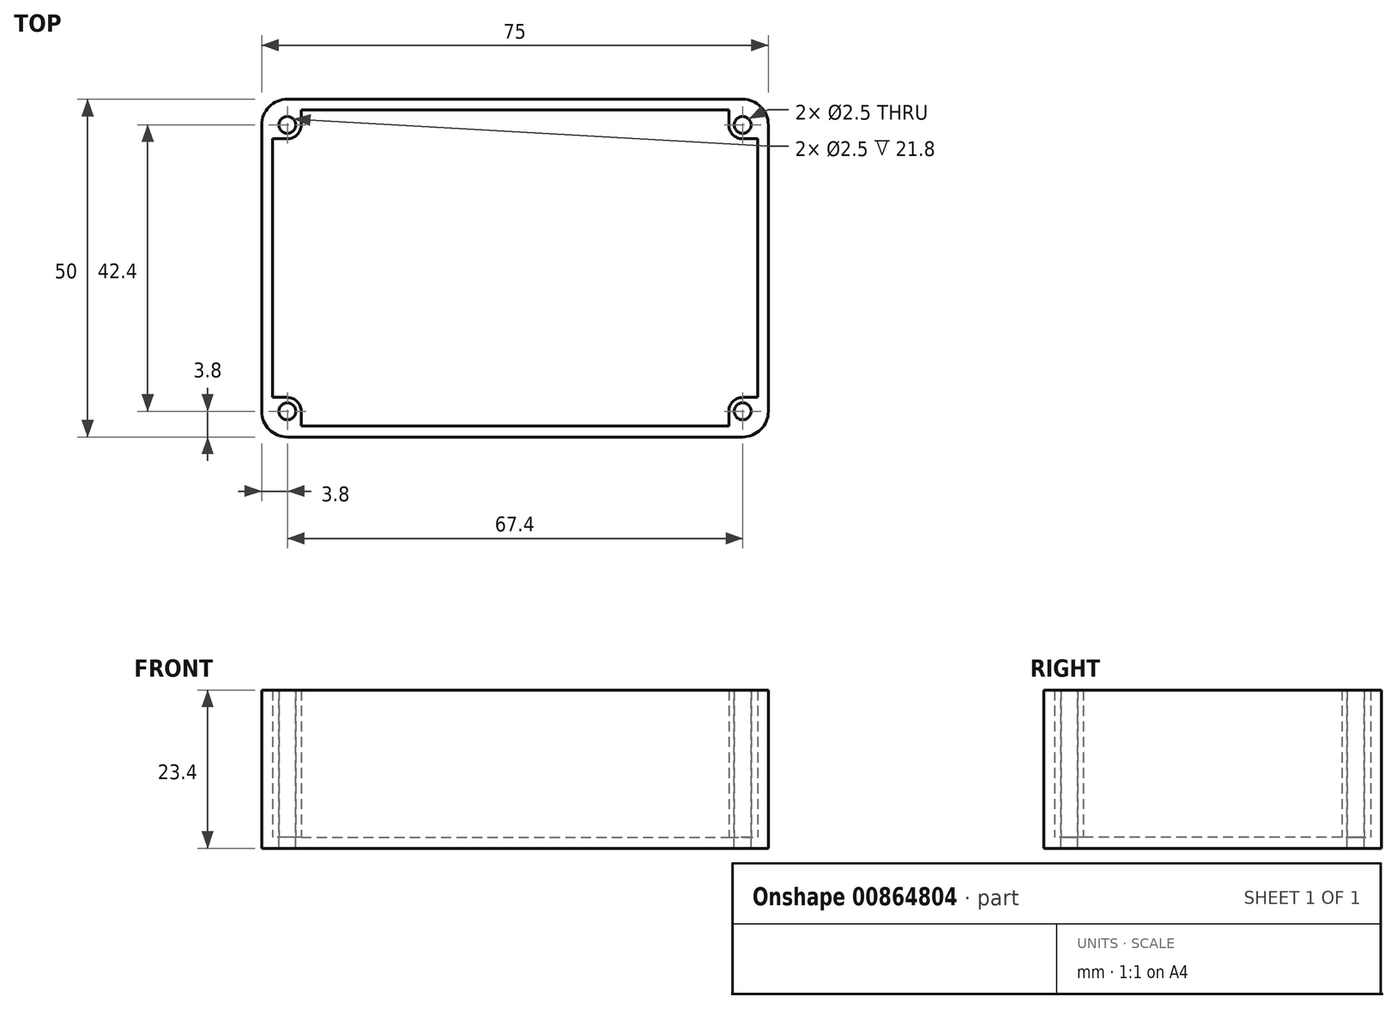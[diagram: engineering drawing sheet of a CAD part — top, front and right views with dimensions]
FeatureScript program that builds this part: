
annotation { "Feature Type Name" : "Feature", "Feature Type Description" : "" }
export const myFeature = defineFeature(function(context is Context, id is Id, definition is map)
    precondition{}
    {
        {
            assignVariable(context, id + "F0", {"name" : "height", "anyValue" : 25});
        }
        {
            assignVariable(context, id + "F1", {"name" : "thickness", "anyValue" : 1.6});
        }
        {
            var Q0;
            Q0=qCreatedBy(makeId("Top.planeOp"),FACE);
            var sketch = newSketch(context, id + "F2", { "sketchPlane" : qUnion([Q0])});
            skLineSegment(sketch, "E0", {"start": v(-37.5, 25) * mm, "end": v(37.5, 25) * mm, "construction": true});
            skLineSegment(sketch, "E1", {"start": v(-37.5, 25) * mm, "end": v(-37.5, -25) * mm, "construction": true});
            skLineSegment(sketch, "E2", {"start": v(-37.5, -25) * mm, "end": v(37.5, -25) * mm, "construction": true});
            skLineSegment(sketch, "E3", {"start": v(37.5, -25) * mm, "end": v(37.5, 25) * mm, "construction": true});
            skLineSegment(sketch, "E4", {"start": v(0, 25) * mm, "end": v(0, 0) * mm, "construction": true});
            skLineSegment(sketch, "E5", {"start": v(0, 0) * mm, "end": v(37.5, 0) * mm, "construction": true});
            skLineSegment(sketch, "E6", {"start": v(0, 0) * mm, "end": v(0, -25) * mm, "construction": true});
            skLineSegment(sketch, "E7", {"start": v(-37.5, 0) * mm, "end": v(0, 0) * mm, "construction": true});
            skLineSegment(sketch, "E8", {"start": v(-33.7, 25) * mm, "end": v(-33.7, -25) * mm, "construction": true});
            skLineSegment(sketch, "E9", {"start": v(-37.5, 21.2) * mm, "end": v(37.5, 21.2) * mm, "construction": true});
            skCircle(sketch, "E10", {"center": v(-33.7, 21.2) * mm, "radius": 1.25 * mm});
            skArc(sketch, "E11", {"start": v(-33.7, 25) * mm, "mid": v(-36.39, 23.89) * mm, "end": v(-37.5, 21.2) * mm});
            skLineSegment(sketch, "E12", {"start": v(-33.7, 25) * mm, "end": v(0, 25) * mm});
            skLineSegment(sketch, "E13", {"start": v(-37.5, 21.2) * mm, "end": v(-37.5, 0) * mm});
            skLineSegment(sketch, "E14", {"start": v(0, 23.4) * mm, "end": v(-31.65, 23.4) * mm});
            skLineSegment(sketch, "E15", {"start": v(-35.9, 19.15) * mm, "end": v(-35.9, 0) * mm});
            skArc(sketch, "E16", {"start": v(-33.7, 19.15) * mm, "mid": v(-32.25, 19.75) * mm, "end": v(-31.65, 21.2) * mm});
            skLineSegment(sketch, "E17", {"start": v(-31.65, 21.2) * mm, "end": v(-31.65, 23.4) * mm});
            skLineSegment(sketch, "E18", {"start": v(-33.7, 19.15) * mm, "end": v(-35.9, 19.15) * mm});
            skCircle(sketch, "E19.MirrorC", {"center": v(33.7, 21.2) * mm, "radius": 1.25 * mm});
            skArc(sketch, "E20.MirrorCS", {"start": v(33.7, 19.15) * mm, "mid": v(32.25, 19.75) * mm, "end": v(31.65, 21.2) * mm});
            skLineSegment(sketch, "E21.MirrorCS", {"start": v(33.7, 19.15) * mm, "end": v(35.9, 19.15) * mm});
            skLineSegment(sketch, "E22.MirrorCS", {"start": v(35.9, 19.15) * mm, "end": v(35.9, 0) * mm});
            skLineSegment(sketch, "E23.MirrorCS", {"start": v(31.65, 21.2) * mm, "end": v(31.65, 23.4) * mm});
            skLineSegment(sketch, "E24.MirrorCS", {"start": v(0, 23.4) * mm, "end": v(31.65, 23.4) * mm});
            skArc(sketch, "E25.MirrorCS", {"start": v(33.7, 25) * mm, "mid": v(36.39, 23.89) * mm, "end": v(37.5, 21.2) * mm});
            skLineSegment(sketch, "E26.MirrorCS", {"start": v(33.7, 25) * mm, "end": v(0, 25) * mm});
            skLineSegment(sketch, "E27.MirrorCS", {"start": v(37.5, 21.2) * mm, "end": v(37.5, 0) * mm});
            skLineSegment(sketch, "E28.MirrorCS", {"start": v(-37.5, -21.2) * mm, "end": v(-37.5, 0) * mm});
            skLineSegment(sketch, "E29.MirrorCS", {"start": v(-33.7, -25) * mm, "end": v(0, -25) * mm});
            skLineSegment(sketch, "E30.MirrorCS", {"start": v(37.5, -21.2) * mm, "end": v(37.5, 0) * mm});
            skLineSegment(sketch, "E31.MirrorCS", {"start": v(33.7, -25) * mm, "end": v(0, -25) * mm});
            skLineSegment(sketch, "E32.MirrorCS", {"start": v(33.7, -19.15) * mm, "end": v(35.9, -19.15) * mm});
            skCircle(sketch, "E33.MirrorC", {"center": v(33.7, -21.2) * mm, "radius": 1.25 * mm});
            skArc(sketch, "E34.MirrorCS", {"start": v(-33.7, -25) * mm, "mid": v(-36.39, -23.89) * mm, "end": v(-37.5, -21.2) * mm});
            skLineSegment(sketch, "E35.MirrorCS", {"start": v(-35.9, -19.15) * mm, "end": v(-35.9, 0) * mm});
            skLineSegment(sketch, "E36.MirrorCS", {"start": v(-31.65, -21.2) * mm, "end": v(-31.65, -23.4) * mm});
            skLineSegment(sketch, "E37.MirrorCS", {"start": v(-33.7, -19.15) * mm, "end": v(-35.9, -19.15) * mm});
            skLineSegment(sketch, "E38.MirrorCS", {"start": v(0, -23.4) * mm, "end": v(31.65, -23.4) * mm});
            skLineSegment(sketch, "E39.MirrorCS", {"start": v(31.65, -21.2) * mm, "end": v(31.65, -23.4) * mm});
            skArc(sketch, "E40.MirrorCS", {"start": v(33.7, -19.15) * mm, "mid": v(32.25, -19.75) * mm, "end": v(31.65, -21.2) * mm});
            skArc(sketch, "E41.MirrorCS", {"start": v(-33.7, -19.15) * mm, "mid": v(-32.25, -19.75) * mm, "end": v(-31.65, -21.2) * mm});
            skLineSegment(sketch, "E42.MirrorCS", {"start": v(35.9, -19.15) * mm, "end": v(35.9, 0) * mm});
            skLineSegment(sketch, "E43.MirrorCS", {"start": v(0, -23.4) * mm, "end": v(-31.65, -23.4) * mm});
            skArc(sketch, "E44.MirrorCS", {"start": v(33.7, -25) * mm, "mid": v(36.39, -23.89) * mm, "end": v(37.5, -21.2) * mm});
            skCircle(sketch, "E45.MirrorC", {"center": v(-33.7, -21.2) * mm, "radius": 1.25 * mm});
            skSolve(sketch);
        }
        {
            var Q0;
            Q0=makeQuery(id+"F2.imprint","IMPRINT",FACE,{"disambiguationData":[TD([[makeQuery(id+"F2.imprint","IMPRINT",EDGE,{"derivedFrom":sQuery(id+"F2.wireOp",EDGE,"E10")}),-1.0]])]});
            var Q1;
            Q1=makeQuery(id+"F2.imprint","IMPRINT",FACE,{"disambiguationData":[TD([[makeQuery(id+"F2.imprint","IMPRINT",EDGE,{"derivedFrom":sQuery(id+"F2.wireOp",EDGE,"E45.MirrorC")}),-1.0]])]});
            var Q2;
            Q2=makeQuery(id+"F2.imprint","IMPRINT",FACE,{"disambiguationData":[TD([[makeQuery(id+"F2.imprint","IMPRINT",EDGE,{"derivedFrom":sQuery(id+"F2.wireOp",EDGE,"E14")}),1.0]])]});
            var Q3;
            Q3=makeQuery(id+"F2.imprint","IMPRINT",FACE,{"disambiguationData":[TD([[makeQuery(id+"F2.imprint","IMPRINT",EDGE,{"derivedFrom":sQuery(id+"F2.wireOp",EDGE,"E33.MirrorC")}),1.0]])]});
            var Q4;
            Q4=makeQuery(id+"F2.imprint","IMPRINT",FACE,{"disambiguationData":[TD([[makeQuery(id+"F2.imprint","IMPRINT",EDGE,{"derivedFrom":sQuery(id+"F2.wireOp",EDGE,"E19.MirrorC")}),-1.0]])]});
            var Q5;
            Q5=makeQuery(id+"F2.imprint","IMPRINT",FACE,{"disambiguationData":[TD([[makeQuery(id+"F2.imprint","IMPRINT",EDGE,{"derivedFrom":sQuery(id+"F2.wireOp",EDGE,"E10")}),1.0]])]});
            extrude(context, id + "F3", {"entities" : qUnion([Q0, Q1, Q2, Q3, Q4, Q5]), "oppositeDirection" : true, "depth" : (getVariable(context, 'thickness')) * mm, "offsetDistance" : 25 * mm});
        }
        {
            var Q0;
            Q0 = qSketchRegion(id + "F2", true);
            extrude(context, id + "F4", {"entities" : qUnion([Q0]), "operationType" : NewBodyOperationType.ADD, "depth" : (getVariable(context, 'height') - getVariable(context, 'thickness') * 2) * mm, "offsetDistance" : 25 * mm});
        }
    });
